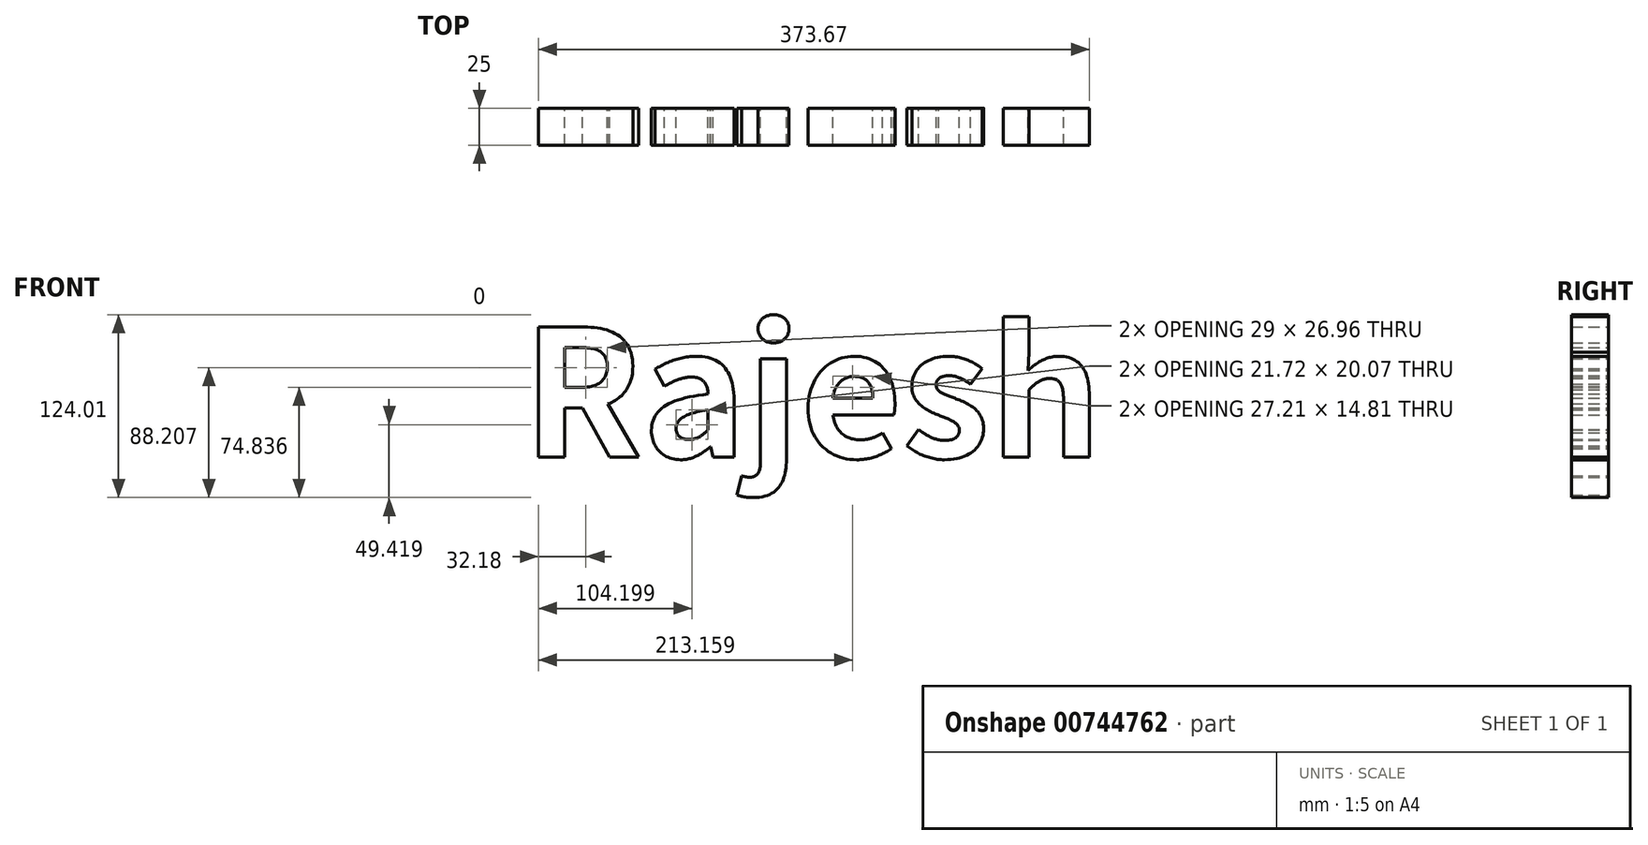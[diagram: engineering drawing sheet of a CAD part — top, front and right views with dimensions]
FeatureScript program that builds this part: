
annotation { "Feature Type Name" : "Feature", "Feature Type Description" : "" }
export const myFeature = defineFeature(function(context is Context, id is Id, definition is map)
    precondition{}
    {
        {
            var Q0;
            Q0=qCreatedBy(makeId("Front.planeOp"),FACE);
            var sketch = newSketch(context, id + "F0", { "sketchPlane" : qUnion([Q0])});
            skText(sketch, "E0", { "text": "Rajesh", "fontName": "NotoSansCJKjp-Bold.otf"});
            const initialGuessF0  = {"E0": [-0.16014, -0.0258, 1, 0, 0.08593]};
            skSetInitialGuess(sketch, initialGuessF0);
            skSolve(sketch);
        }
        {
            var Q0;
            Q0 = qSketchRegion(id + "F0", true);
            extrude(context, id + "F1", {"entities" : qUnion([Q0]), "depth" : 25 * mm, "offsetDistance" : 25 * mm});
        }
    });
